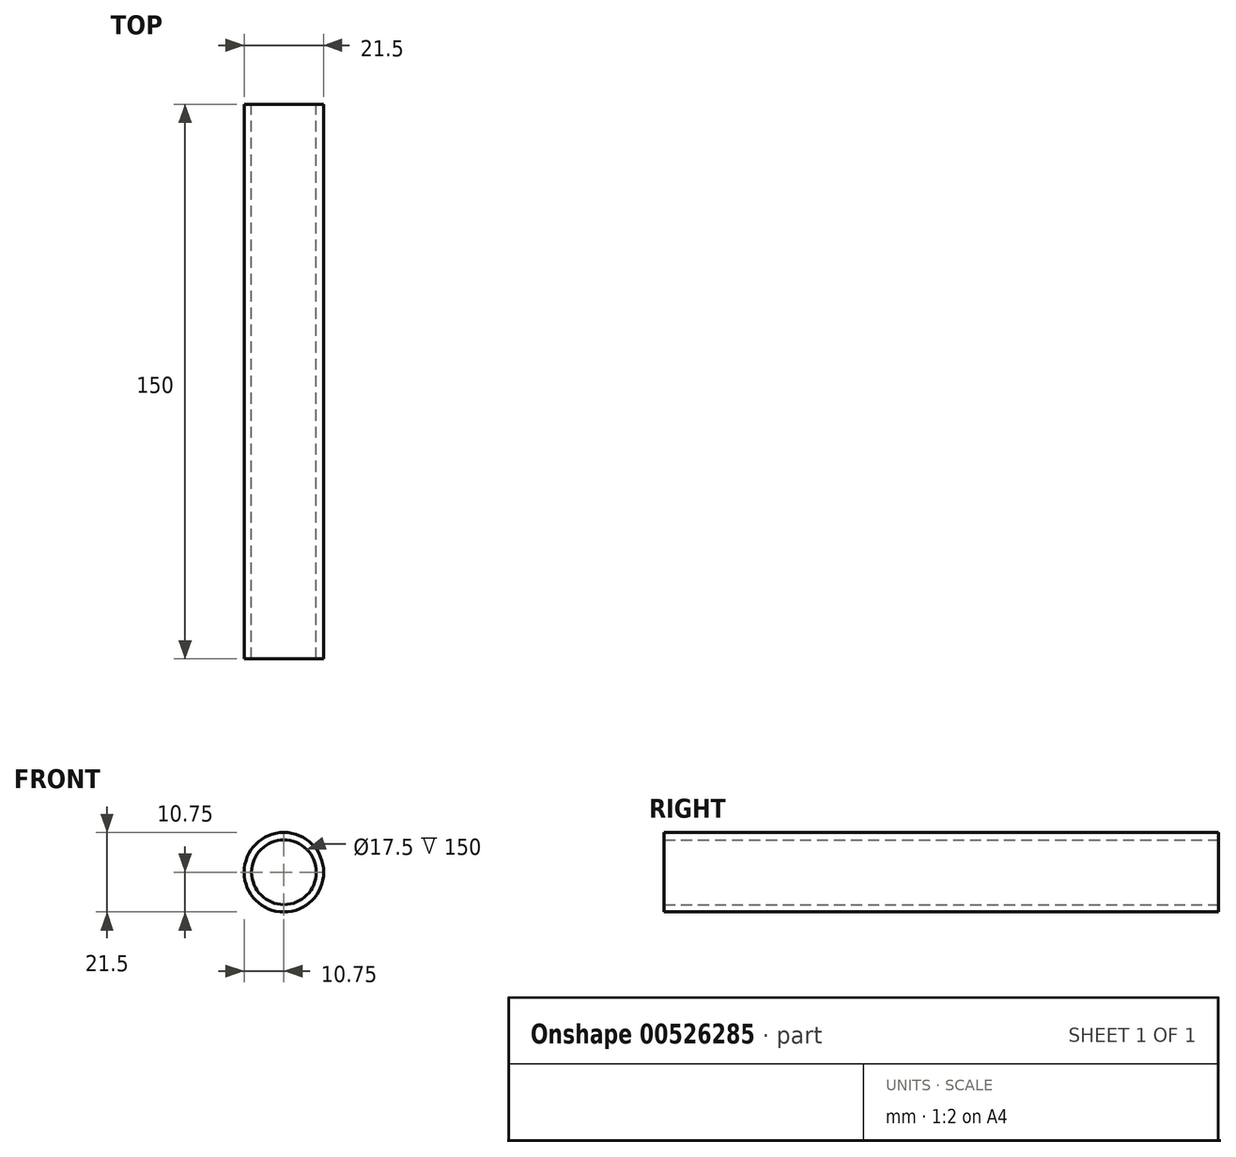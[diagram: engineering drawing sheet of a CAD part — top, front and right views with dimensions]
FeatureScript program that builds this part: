
annotation { "Feature Type Name" : "Feature", "Feature Type Description" : "" }
export const myFeature = defineFeature(function(context is Context, id is Id, definition is map)
    precondition{}
    {
        {
            var Q0;
            Q0=qCreatedBy(makeId("Front.planeOp"),FACE);
            var sketch = newSketch(context, id + "F0", { "sketchPlane" : qUnion([Q0])});
            skCircle(sketch, "E0", {"center": v(0, 0) * mm, "radius": 10.75 * mm});
            skCircle(sketch, "E1", {"center": v(0, 0) * mm, "radius": 8.75 * mm});
            skSolve(sketch);
        }
        {
            var Q0;
            Q0=qSketchRegion(id+"F0",true);
            extrude(context, id + "F1", {"entities" : qUnion([Q0]), "depth" : 150 * mm, "offsetDistance" : 25 * mm});
        }
    });
